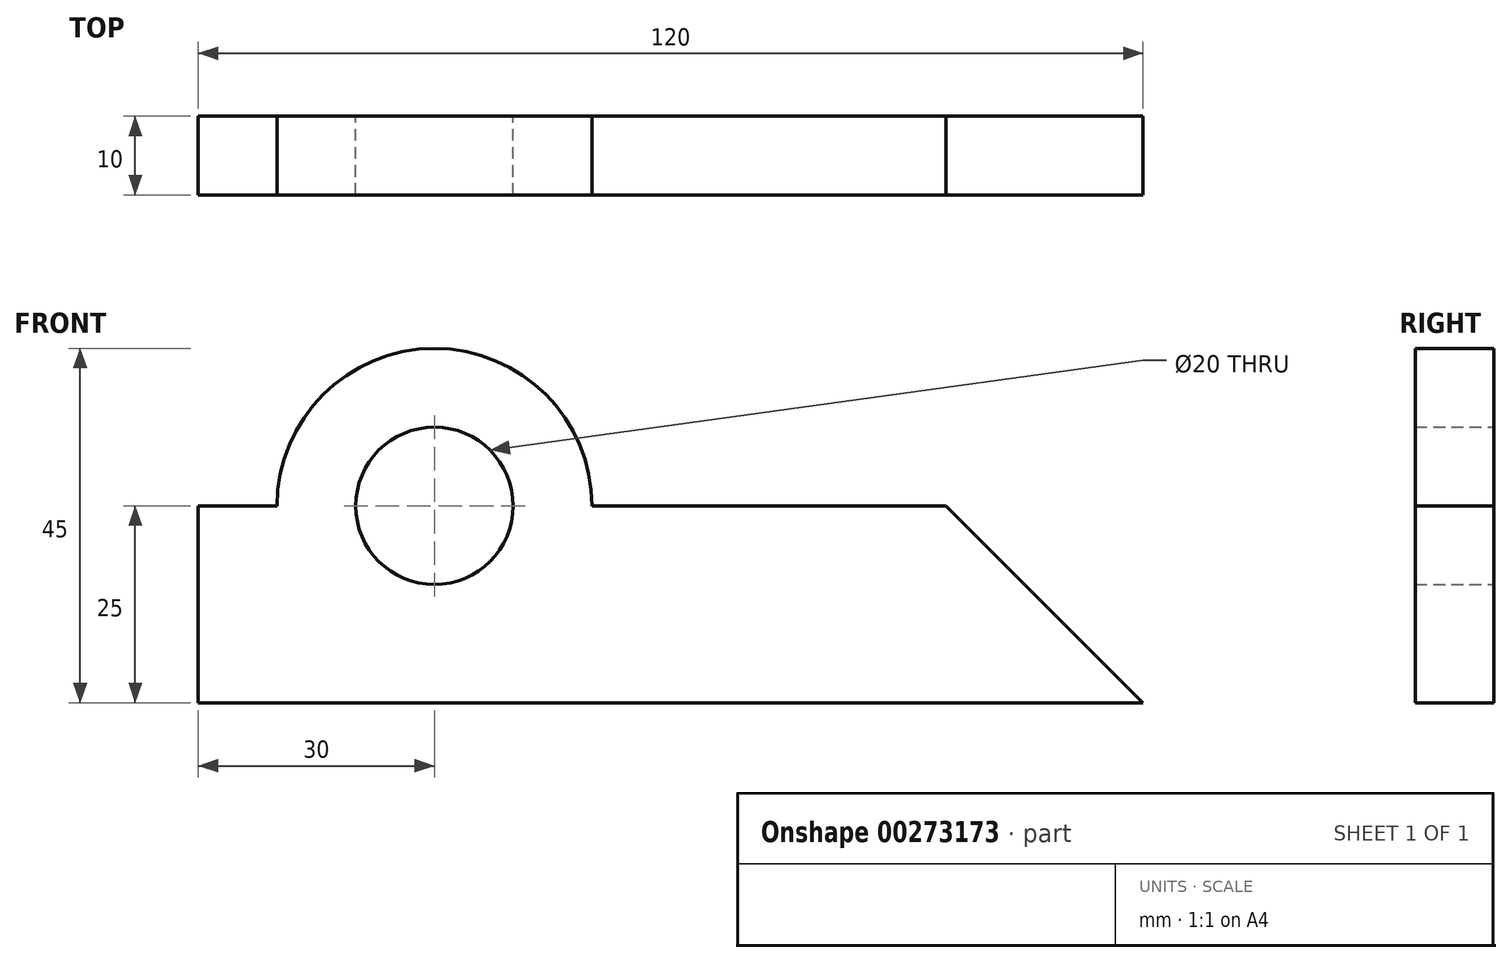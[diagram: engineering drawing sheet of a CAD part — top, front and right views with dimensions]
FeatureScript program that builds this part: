
annotation { "Feature Type Name" : "Feature", "Feature Type Description" : "" }
export const myFeature = defineFeature(function(context is Context, id is Id, definition is map)
    precondition{}
    {
        {
            var Q0;
            Q0=qCreatedBy(makeId("Front.planeOp"),FACE);
            var sketch = newSketch(context, id + "F0", { "sketchPlane" : qUnion([Q0])});
            skLineSegment(sketch, "E0", {"start": v(0, 0) * mm, "end": v(120, 0) * mm});
            skLineSegment(sketch, "E1", {"start": v(0, 0) * mm, "end": v(0, 25) * mm});
            skLineSegment(sketch, "E2", {"start": v(0, 25) * mm, "end": v(10, 25) * mm});
            skArc(sketch, "E3", {"start": v(50, 25) * mm, "mid": v(30, 45) * mm, "end": v(10, 25) * mm});
            skLineSegment(sketch, "E4", {"start": v(50, 25) * mm, "end": v(95, 25) * mm});
            skLineSegment(sketch, "E5", {"start": v(95, 25) * mm, "end": v(120, 0) * mm});
            skCircle(sketch, "E6", {"center": v(30, 25) * mm, "radius": 10 * mm});
            skSolve(sketch);
        }
        {
            var Q0;
            Q0 = qSketchRegion(id + "F0", true);
            extrude(context, id + "F1", {"entities" : qUnion([Q0]), "depth" : 10 * mm});
        }
    });
